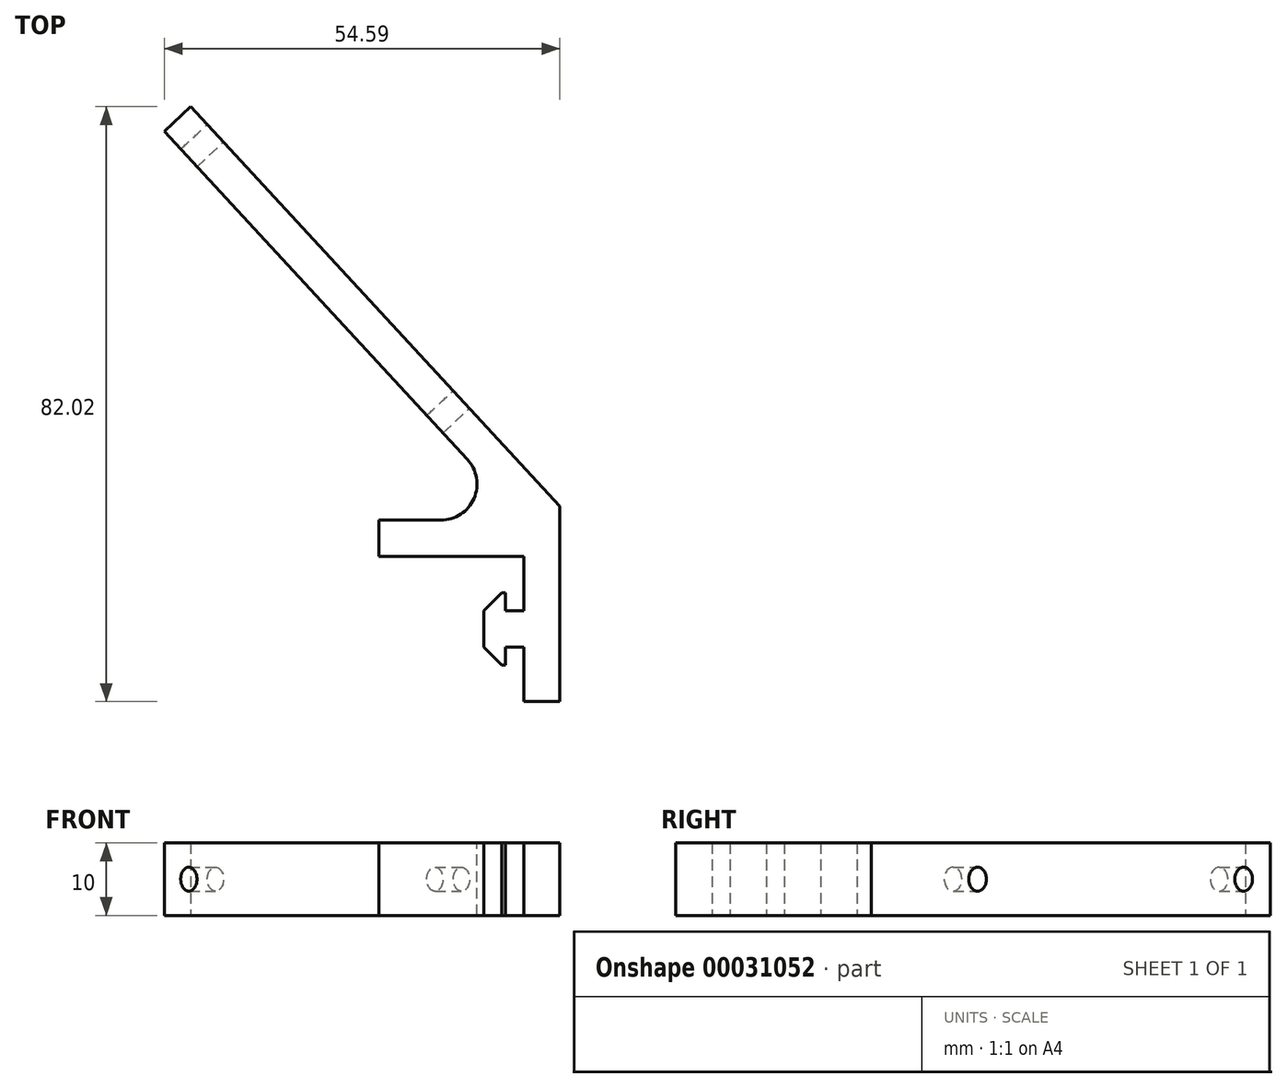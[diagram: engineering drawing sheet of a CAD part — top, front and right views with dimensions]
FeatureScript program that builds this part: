
annotation { "Feature Type Name" : "Feature", "Feature Type Description" : "" }
export const myFeature = defineFeature(function(context is Context, id is Id, definition is map)
    precondition{}
    {
        {
            var Q0;
            Q0=qCreatedBy(makeId("Top.planeOp"),FACE);
            var sketch = newSketch(context, id + "F0", { "sketchPlane" : qUnion([Q0])});
            skLineSegment(sketch, "E0", {"start": v(-25, 20) * mm, "end": v(-5, 20) * mm});
            skLineSegment(sketch, "E1", {"start": v(-5, 20) * mm, "end": v(-5, 12.5) * mm});
            skLineSegment(sketch, "E2", {"start": v(-5, 12.5) * mm, "end": v(-7.5, 12.5) * mm});
            skLineSegment(sketch, "E3", {"start": v(-7.5, 12.5) * mm, "end": v(-7.5, 15) * mm});
            skLineSegment(sketch, "E4", {"start": v(-7.5, 15) * mm, "end": v(-8, 15) * mm});
            skLineSegment(sketch, "E5", {"start": v(-8, 15) * mm, "end": v(-10.5, 12.5) * mm});
            skLineSegment(sketch, "E6", {"start": v(-10.5, 12.5) * mm, "end": v(-10.5, 7.5) * mm});
            skLineSegment(sketch, "E7", {"start": v(-10.5, 7.5) * mm, "end": v(-8, 5) * mm});
            skLineSegment(sketch, "E8", {"start": v(-8, 5) * mm, "end": v(-7.5, 5) * mm});
            skLineSegment(sketch, "E9", {"start": v(-7.5, 5) * mm, "end": v(-7.5, 7.5) * mm});
            skLineSegment(sketch, "E10", {"start": v(-7.5, 7.5) * mm, "end": v(-5, 7.5) * mm});
            skLineSegment(sketch, "E11", {"start": v(-5, 7.5) * mm, "end": v(-5, 0) * mm});
            skLineSegment(sketch, "E12", {"start": v(-5, 0) * mm, "end": v(0, 0) * mm});
            skLineSegment(sketch, "E13", {"start": v(0, 0) * mm, "end": v(0, 26.96) * mm});
            skLineSegment(sketch, "E14", {"start": v(0, 26.96) * mm, "end": v(-50.92, 82.02) * mm});
            skLineSegment(sketch, "E15", {"start": v(-50.92, 82.02) * mm, "end": v(-54.6, 78.63) * mm});
            skLineSegment(sketch, "E16", {"start": v(-54.6, 78.63) * mm, "end": v(-5, 25) * mm});
            skLineSegment(sketch, "E17", {"start": v(-5, 25) * mm, "end": v(-25, 25) * mm});
            skLineSegment(sketch, "E18", {"start": v(-25, 25) * mm, "end": v(-25, 20) * mm});
            skSolve(sketch);
        }
        {
            var Q0;
            Q0=makeQuery(id+"F0.imprint","IMPRINT",FACE,{"disambiguationData":[TD([[makeQuery(id+"F0.imprint","IMPRINT",EDGE,{"derivedFrom":sQuery(id+"F0.wireOp",EDGE,"E0")}),1.0]])]});
            extrude(context, id + "F1", {"entities" : qUnion([Q0]), "depth" : 10 * mm});
        }
        {
            var Q0;
            Q0=makeQuery(id+"F1.opExtrude","SWEPT_EDGE",EDGE,{"disambiguationData":[OSD([sQuery(id+"F0.wireOp",EDGE,"E16"),sQuery(id+"F0.wireOp",EDGE,"E17")])]});
            fillet(context, id + "F2", {"entities" : qUnion([Q0]), "radius" : 5 * mm, "tangentPropagation" : true, "allowEdgeOverflow" : false});
        }
        {
            var Q0;
            Q0=makeQuery(id+"F1.opExtrude","SWEPT_FACE",FACE,{"disambiguationData":[OSD([sQuery(id+"F0.wireOp",EDGE,"E14")])]});
            var sketch = newSketch(context, id + "F3", { "sketchPlane" : qUnion([Q0])});
            skCircle(sketch, "E19", {"center": v(89.8, 5) * mm, "radius": 1.65 * mm});
            skCircle(sketch, "E20", {"center": v(39.8, 5) * mm, "radius": 1.65 * mm});
            skSolve(sketch);
        }
        {
            var Q0;
            Q0=makeQuery(id+"F3.imprint","IMPRINT",FACE,{"disambiguationData":[TD([[makeQuery(id+"F3.imprint","IMPRINT",EDGE,{"derivedFrom":sQuery(id+"F3.wireOp",EDGE,"E19")}),1.0]])]});
            extrude(context, id + "F4", {"entities" : qUnion([Q0]), "operationType" : NewBodyOperationType.REMOVE, "endBound" : BoundingType.THROUGH_ALL, "oppositeDirection" : true, "depth" : 25 * mm});
        }
        {
            var Q0;
            Q0=makeQuery(id+"F3.imprint","IMPRINT",FACE,{"disambiguationData":[TD([[makeQuery(id+"F3.imprint","IMPRINT",EDGE,{"derivedFrom":sQuery(id+"F3.wireOp",EDGE,"E20")}),1.0]])]});
            extrude(context, id + "F5", {"entities" : qUnion([Q0]), "operationType" : NewBodyOperationType.REMOVE, "oppositeDirection" : true, "depth" : 25 * mm});
        }
    });
